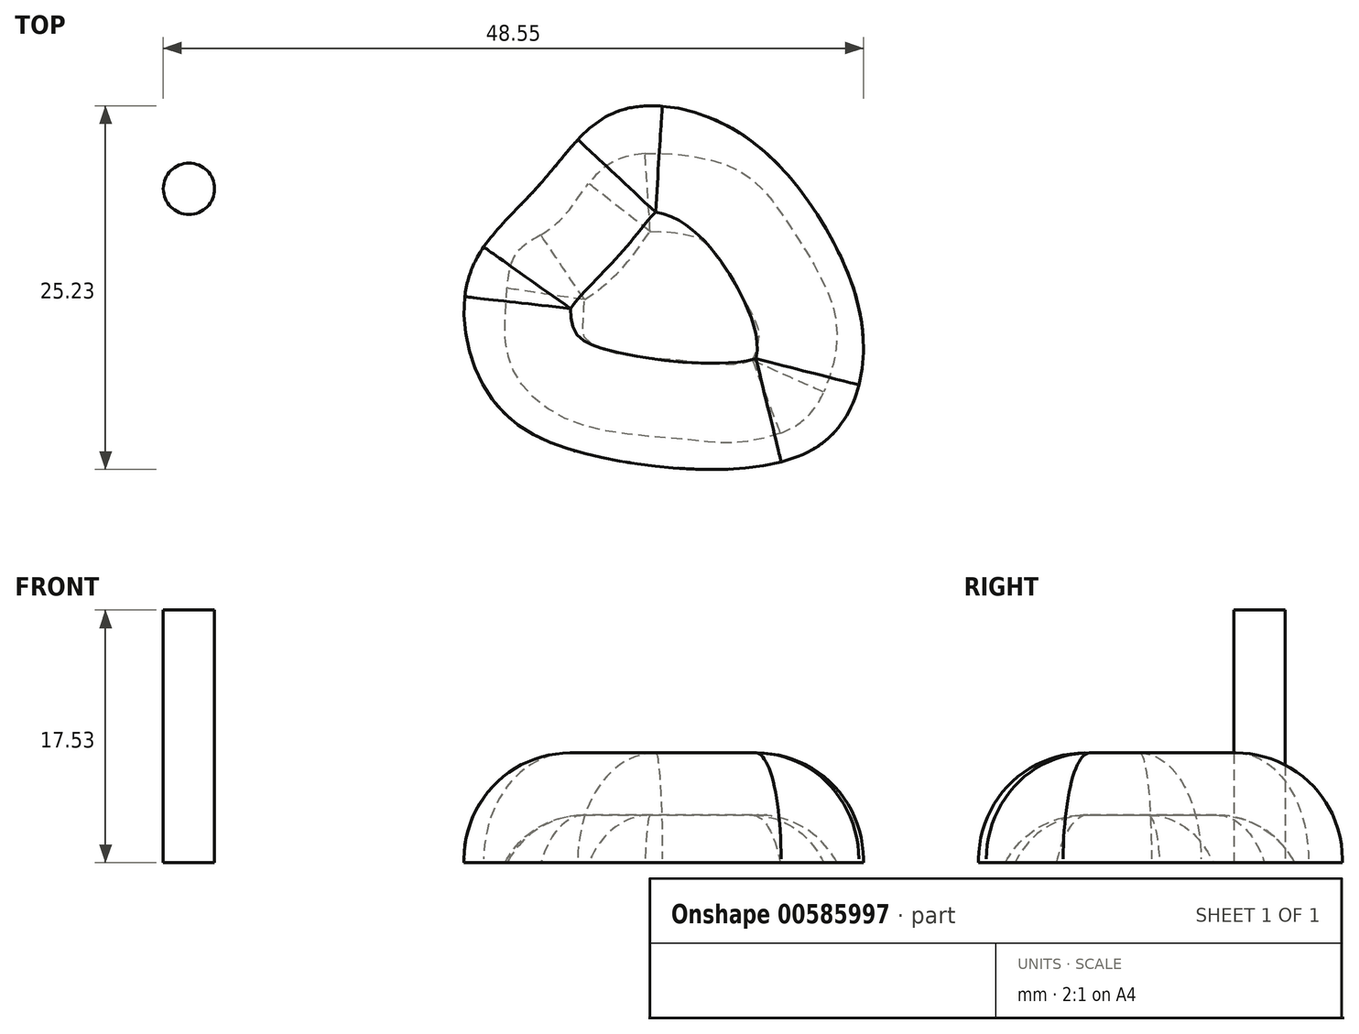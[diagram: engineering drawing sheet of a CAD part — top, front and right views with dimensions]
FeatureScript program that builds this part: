
annotation { "Feature Type Name" : "Feature", "Feature Type Description" : "" }
export const myFeature = defineFeature(function(context is Context, id is Id, definition is map)
    precondition{}
    {
        {
            var Q0;
            Q0=qCreatedBy(makeId("Top.planeOp"),FACE);
            var sketch = newSketch(context, id + "F0", { "sketchPlane" : qUnion([Q0])});
            skCircle(sketch, "E0", {"center": v(-55.93, 41.65) * mm, "radius": 1.78 * mm});
            skSolve(sketch);
        }
        {
            var Q0;
            Q0=makeQuery(id+"F0.imprint","IMPRINT",FACE,{"disambiguationData":[TD([[makeQuery(id+"F0.imprint","IMPRINT",EDGE,{"derivedFrom":sQuery(id+"F0.wireOp",EDGE,"E0")}),1.0]])]});
            extrude(context, id + "F1", {"entities" : qUnion([Q0]), "depth" : 17.53 * mm, "offsetDistance" : 25.4 * mm});
        }
        {
            var Q0;
            Q0=qCreatedBy(makeId("Top.planeOp"),FACE);
            var sketch = newSketch(context, id + "F2", { "sketchPlane" : qUnion([Q0])});
            skFitSpline(sketch, "E1", {"points": [v(-31.4, 42.15) * mm, v(-35.96, 36.85) * mm, v(-36.72, 31.54) * mm, v(-33.94, 25.97) * mm, v(-25.6, 22.69) * mm, v(-12.45, 23.7) * mm, v(-9.16, 30.27) * mm, v(-11.19, 37.86) * mm, v(-18.01, 45.7) * mm, v(-26.35, 46.96) * mm, v(-31.4, 42.15) * mm]});
            skSolve(sketch);
        }
        {
            var Q0;
            Q0=makeQuery(id+"F2.imprint","IMPRINT",FACE,{"disambiguationData":[TD([[makeQuery(id+"F2.imprint","IMPRINT",EDGE,{"derivedFrom":sQuery(id+"F2.wireOp",EDGE,"E1")}),1.0]])]});
            extrude(context, id + "F3", {"entities" : qUnion([Q0]), "depth" : 7.62 * mm, "offsetDistance" : 25.4 * mm});
        }
        {
            var Q0;
            Q0=makeQuery(id+"F3.opExtrude","CAP_EDGE",EDGE,{"disambiguationData":[OSD([sQuery(id+"F2.wireOp",EDGE,"E1")])],"isStart":false});
            fillet(context, id + "F4", {"entities" : qUnion([Q0]), "radius" : 7.37 * mm, "tangentPropagation" : true, "allowEdgeOverflow" : false});
        }
        {
            var Q0;
            Q0=makeQuery(id+"F3.opExtrude","CAP_FACE",FACE,{"disambiguationData":[OSD([sQuery(id+"F2.wireOp",EDGE,"E1")])],"isStart":true});
            var sketch = newSketch(context, id + "F5", { "sketchPlane" : qUnion([Q0])});
            skFitSpline(sketch, "E2", {"points": [v(-29.04, -25.39) * mm, v(-33.08, -28.42) * mm, v(-34, -31.46) * mm, v(-33.91, -34.03) * mm, v(-33.36, -36.98) * mm, v(-31.52, -38.45) * mm, v(-29.77, -39.92) * mm, v(-28.12, -42.12) * mm, v(-25.91, -43.78) * mm, v(-21.5, -43.96) * mm, v(-17.27, -42.58) * mm, v(-14.51, -39.46) * mm, v(-12.3, -35.87) * mm, v(-11.02, -32.2) * mm, v(-11.66, -28.15) * mm, v(-13.6, -25.39) * mm, v(-17.36, -24.1) * mm, v(-19.94, -24.1) * mm, v(-22.79, -24.38) * mm, v(-29.04, -25.39) * mm]});
            skSolve(sketch);
        }
        {
            var Q0;
            Q0=makeQuery(id+"F5.imprint","IMPRINT",FACE,{"disambiguationData":[TD([[makeQuery(id+"F5.imprint","IMPRINT",EDGE,{"derivedFrom":sQuery(id+"F5.wireOp",EDGE,"E2")}),1.0]])]});
            extrude(context, id + "F6", {"entities" : qUnion([Q0]), "operationType" : NewBodyOperationType.REMOVE, "oppositeDirection" : true, "depth" : 3.3 * mm, "offsetDistance" : 25.4 * mm});
        }
        {
            var Q0;
            Q0=makeQuery(id+"F6.boolean.opBoolean","COPY",EDGE,{"derivedFrom":makeQuery(id+"F6.opExtrude","CAP_EDGE",EDGE,{"disambiguationData":[OSD([sQuery(id+"F5.wireOp",EDGE,"E2")])],"isStart":false})});
            fillet(context, id + "F7", {"entities" : qUnion([Q0]), "radius" : 6.1 * mm, "tangentPropagation" : true, "allowEdgeOverflow" : false});
        }
    });
